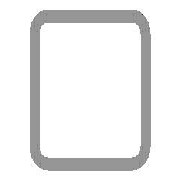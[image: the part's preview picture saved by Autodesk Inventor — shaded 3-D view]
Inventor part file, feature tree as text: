
AUTODESK INVENTOR PART (.ipt)
format: ipt  version: 2025.1 (Build 291241020, 241B)  size: 137,216 bytes
history: native  units: mm (DEFAULTED — no unit token found)
features: other x3, sketch x1, plane x1
ambient origin geometry x8: Origin, YZ Plane, XZ Plane, XY Plane, X Axis, Y Axis, Z Axis, Center Point
bodies: Solid1 (feature_tree), Body (feature_tree)
feature tree (5):
  other  "Driven Length"
  other  "Start plane"
  other  "End plane"
  sketch  "Sketch3"  dims[d3=6800.0mm d4=0.0mm d7=6.0mm d10=100.0mm d11=100.0mm d12=4.0mm d13=-0.0mm d14=6800.0mm d15=50.0mm d16=50.0mm d17=90.0deg d18=6800.0mm d19=4.0mm d20=4.0mm]
  plane  "Work Plane3"
